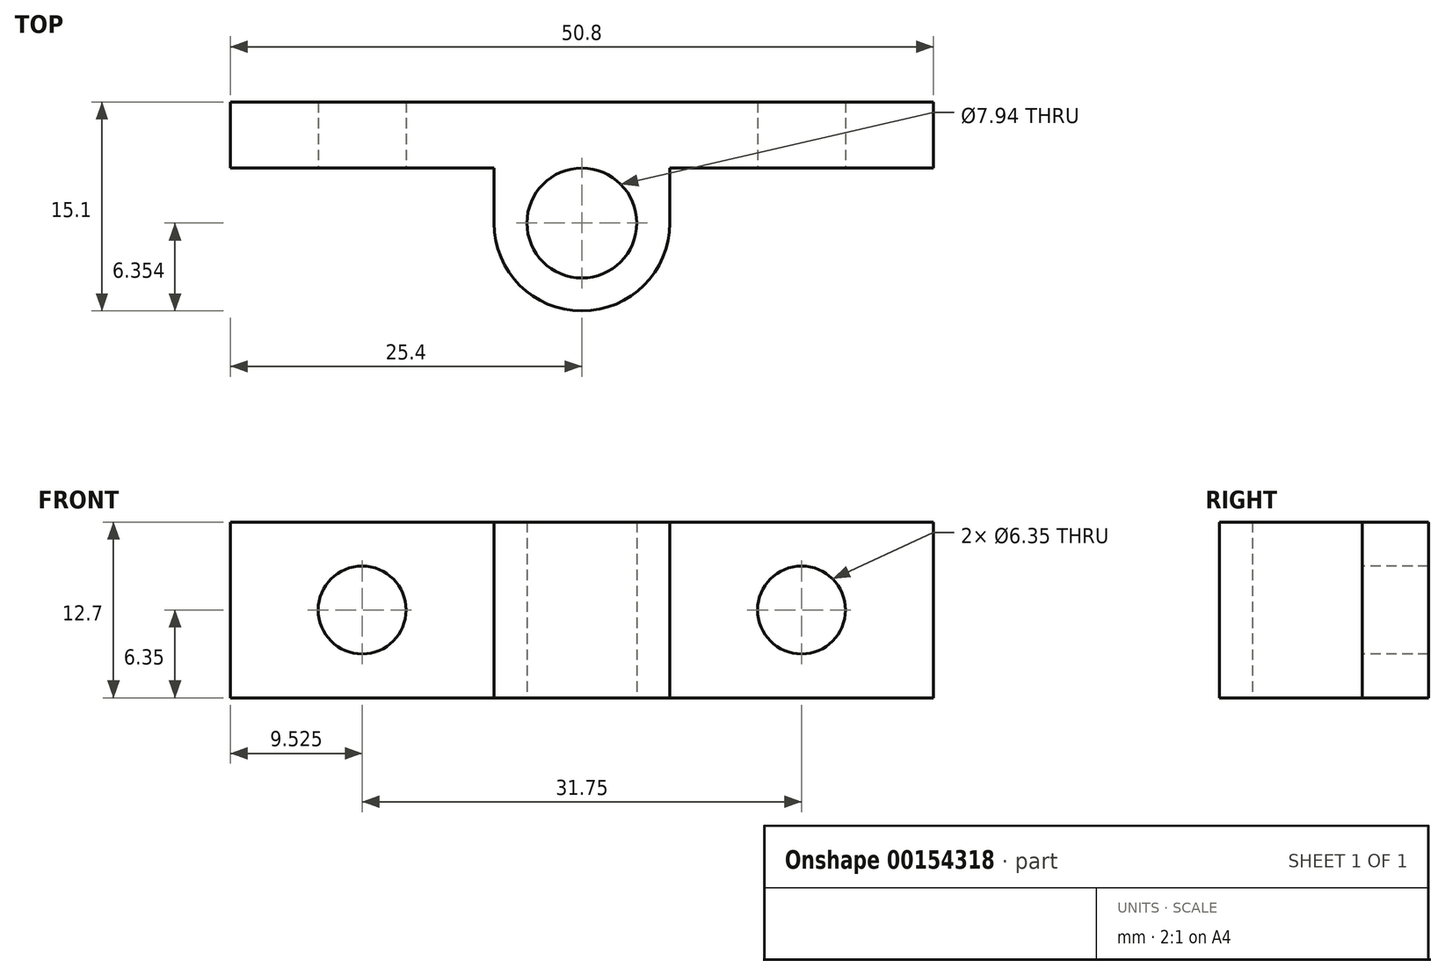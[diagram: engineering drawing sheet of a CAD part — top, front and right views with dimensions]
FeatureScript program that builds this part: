
annotation { "Feature Type Name" : "Feature", "Feature Type Description" : "" }
export const myFeature = defineFeature(function(context is Context, id is Id, definition is map)
    precondition{}
    {
        {
            var Q0;
            Q0=qCreatedBy(makeId("Top.planeOp"),FACE);
            var sketch = newSketch(context, id + "F0", { "sketchPlane" : qUnion([Q0])});
            skLineSegment(sketch, "E0.bottom", {"start": v(-25.4, -2.39) * mm, "end": v(25.4, -2.39) * mm});
            skLineSegment(sketch, "E0.top", {"start": v(-25.4, 2.39) * mm, "end": v(25.4, 2.39) * mm});
            skLineSegment(sketch, "E0.left", {"start": v(-25.4, -2.39) * mm, "end": v(-25.4, 2.39) * mm});
            skLineSegment(sketch, "E0.right", {"start": v(25.4, -2.39) * mm, "end": v(25.4, 2.39) * mm});
            skPoint(sketch, "E0.middle", {"position": v(0, 0) * mm});
            skCircle(sketch, "E1", {"center": v(0, -6.36) * mm, "radius": 3.97 * mm});
            skArc(sketch, "E2", {"start": v(-6.35, -6.36) * mm, "mid": v(0, -12.7) * mm, "end": v(6.35, -6.36) * mm});
            skLineSegment(sketch, "E3", {"start": v(6.35, -6.36) * mm, "end": v(6.35, -2.39) * mm});
            skLineSegment(sketch, "E4", {"start": v(-6.35, -6.36) * mm, "end": v(-6.35, -2.39) * mm});
            skSolve(sketch);
        }
        {
            var Q0;
            Q0 = qSketchRegion(id + "F0", true);
            extrude(context, id + "F1", {"entities" : qUnion([Q0]), "depth" : 12.7 * mm});
        }
        {
            var Q0;
            {var subQ0=sQuery(id+"F0.wireOp",EDGE,"E0.bottom");Q0=makeQuery(id+"F1.opExtrude","SWEPT_FACE",FACE,{"disambiguationData":[OSD([subQ0]),TDD([makeQuery(id+"F0.imprint","IMPRINT",EDGE,{"disambiguationData":[TD([[makeQuery(id+"F0.imprint","INTERSECT",VERTEX,{"derivedFrom":[subQ0,sQuery(id+"F0.wireOp",EDGE,"E0.right")]}),1.0]])],"derivedFrom":subQ0})])]});}
            var sketch = newSketch(context, id + "F2", { "sketchPlane" : qUnion([Q0])});
            skCircle(sketch, "E5", {"center": v(-15.88, 6.35) * mm, "radius": 3.18 * mm});
            skLineSegment(sketch, "E6", {"start": v(-25.4, 6.35) * mm, "end": v(-6.35, 6.35) * mm});
            skLineSegment(sketch, "E7", {"start": v(-15.88, 12.7) * mm, "end": v(-15.88, 0) * mm});
            skCircle(sketch, "E8.MirrorC", {"center": v(15.88, 6.35) * mm, "radius": 3.18 * mm});
            skSolve(sketch);
        }
        {
            var Q0;
            Q0 = qSketchRegion(id + "F2", true);
            var Q1;
            Q1=makeQuery(id+"F1.opExtrude","SWEPT_FACE",FACE,{"disambiguationData":[OSD([sQuery(id+"F0.wireOp",EDGE,"E0.top")])]});
            extrude(context, id + "F3", {"entities" : qUnion([Q0]), "operationType" : NewBodyOperationType.REMOVE, "endBound" : BoundingType.UP_TO_SURFACE, "oppositeDirection" : true, "endBoundEntityFace" : qUnion([Q1]), "depth" : 25.4 * mm});
        }
    });
